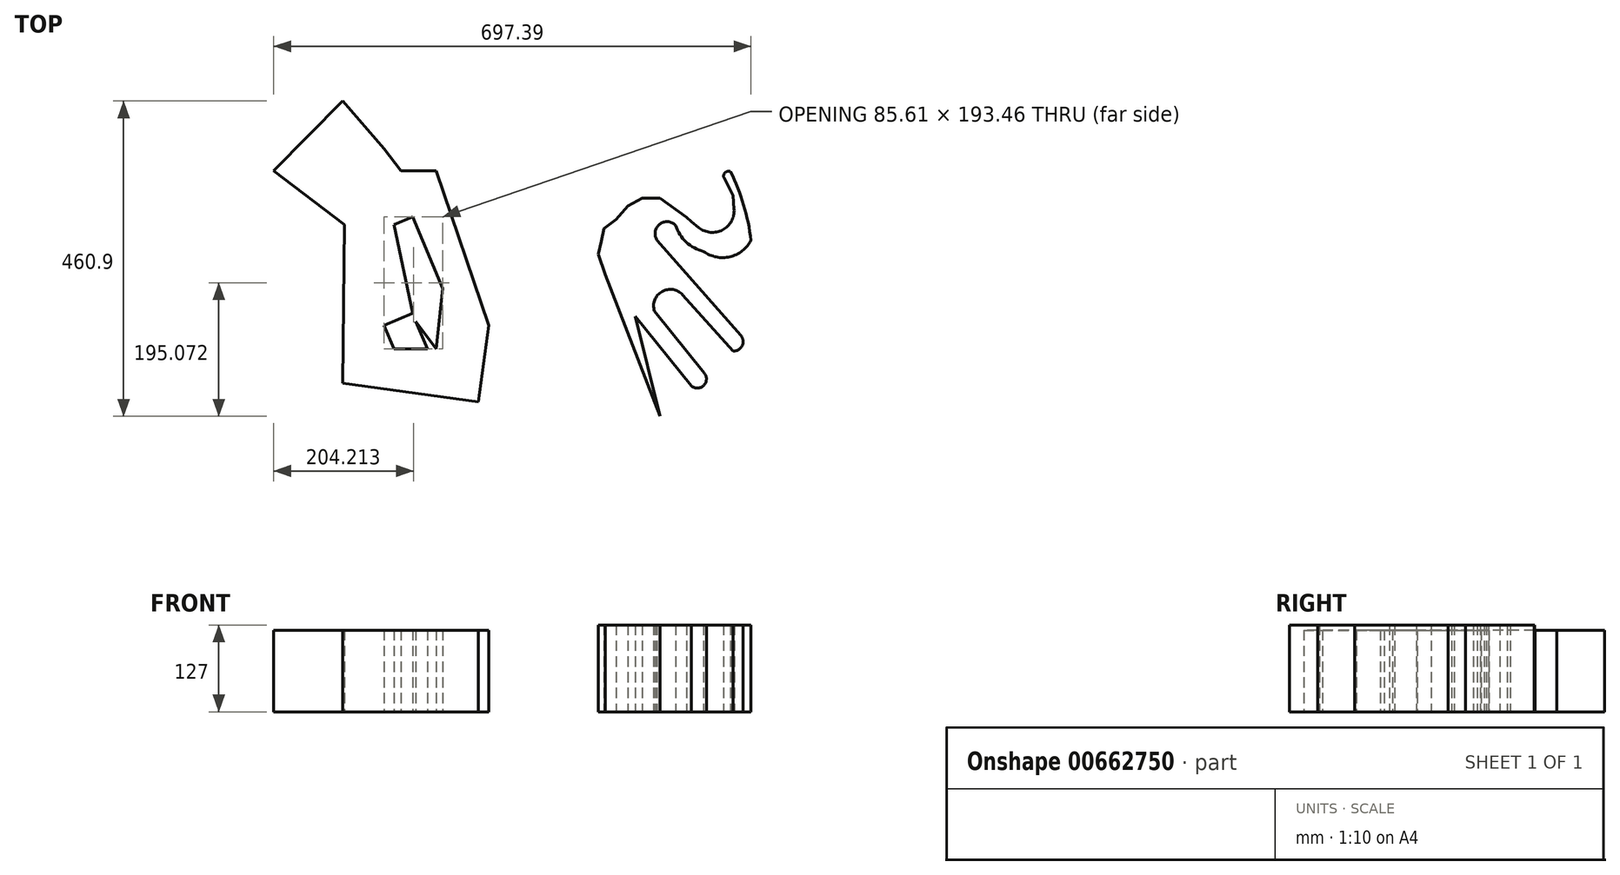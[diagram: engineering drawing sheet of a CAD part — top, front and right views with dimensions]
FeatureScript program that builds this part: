
annotation { "Feature Type Name" : "Feature", "Feature Type Description" : "" }
export const myFeature = defineFeature(function(context is Context, id is Id, definition is map)
    precondition{}
    {
        {
            var Q0;
            Q0=qCreatedBy(makeId("Top.planeOp"),FACE);
            var sketch = newSketch(context, id + "F0", { "sketchPlane" : qUnion([Q0])});
            skLineSegment(sketch, "E0", {"start": v(47.23, 61.57) * mm, "end": v(53.85, 55.23) * mm});
            skLineSegment(sketch, "E1", {"start": v(53.85, 55.23) * mm, "end": v(64.9, 46.36) * mm});
            skArc(sketch, "E2", {"start": v(64.9, 46.36) * mm, "mid": v(99.64, 43.04) * mm, "end": v(116.5, 73.6) * mm});
            skLineSegment(sketch, "E3", {"start": v(116.5, 73.6) * mm, "end": v(114.97, 93.25) * mm});
            skLineSegment(sketch, "E4", {"start": v(114.97, 93.25) * mm, "end": v(101.97, 118.57) * mm});
            skArc(sketch, "E5", {"start": v(111.25, 128.16) * mm, "mid": v(103.17, 126.7) * mm, "end": v(101.97, 118.57) * mm});
            skArc(sketch, "E6", {"start": v(141.26, 27.78) * mm, "mid": v(130.43, 79.22) * mm, "end": v(111.25, 128.16) * mm});
            skArc(sketch, "E7", {"start": v(71.92, 11.46) * mm, "mid": v(110.32, 3.76) * mm, "end": v(141.26, 27.78) * mm});
            skArc(sketch, "E8", {"start": v(31.18, 49.76) * mm, "mid": v(46.48, 25.22) * mm, "end": v(71.92, 11.46) * mm});
            skArc(sketch, "E9", {"start": v(31.18, 49.76) * mm, "mid": v(7.54, 51.2) * mm, "end": v(3.97, 27.78) * mm});
            skLineSegment(sketch, "E10", {"start": v(3.97, 27.78) * mm, "end": v(126.28, -111.28) * mm});
            skArc(sketch, "E11", {"start": v(114.82, -133.98) * mm, "mid": v(128.22, -126.5) * mm, "end": v(126.28, -111.28) * mm});
            skLineSegment(sketch, "E12", {"start": v(114.82, -133.98) * mm, "end": v(41.23, -51.98) * mm});
            skArc(sketch, "E13", {"start": v(41.23, -51.98) * mm, "mid": v(11.1, -47.12) * mm, "end": v(0, -75.54) * mm});
            skLineSegment(sketch, "E14", {"start": v(0, -75.54) * mm, "end": v(73.08, -166.55) * mm});
            skArc(sketch, "E15", {"start": v(54.15, -185.1) * mm, "mid": v(72.02, -184.4) * mm, "end": v(73.08, -166.55) * mm});
            skLineSegment(sketch, "E16", {"start": v(54.15, -185.1) * mm, "end": v(-27.85, -83.4) * mm});
            skLineSegment(sketch, "E17", {"start": v(-27.85, -83.4) * mm, "end": v(-71.92, -22.47) * mm});
            skLineSegment(sketch, "E18", {"start": v(-71.92, -22.47) * mm, "end": v(-81.6, 7.5) * mm});
            skLineSegment(sketch, "E19", {"start": v(-81.6, 7.5) * mm, "end": v(-77.5, 26.8) * mm});
            skLineSegment(sketch, "E20", {"start": v(-77.5, 26.8) * mm, "end": v(-73.68, 45.1) * mm});
            skLineSegment(sketch, "E21", {"start": v(-73.68, 45.1) * mm, "end": v(-56.1, 58.65) * mm});
            skLineSegment(sketch, "E22", {"start": v(-56.1, 58.65) * mm, "end": v(-38.53, 78.1) * mm});
            skLineSegment(sketch, "E23", {"start": v(-38.53, 78.1) * mm, "end": v(-17.84, 89.2) * mm});
            skLineSegment(sketch, "E24", {"start": v(-17.84, 89.2) * mm, "end": v(8.08, 89.2) * mm});
            skLineSegment(sketch, "E25", {"start": v(8.08, 89.2) * mm, "end": v(47.23, 61.57) * mm});
            skLineSegment(sketch, "E26", {"start": v(-71.92, -22.47) * mm, "end": v(8.08, -229.5) * mm});
            skLineSegment(sketch, "E27", {"start": v(8.08, -229.5) * mm, "end": v(-27.85, -83.4) * mm});
            skSolve(sketch);
        }
        {
            var Q0;
            Q0=makeQuery(id+"F0.imprint","IMPRINT",FACE,{"disambiguationData":[TD([[makeQuery(id+"F0.imprint","IMPRINT",EDGE,{"derivedFrom":sQuery(id+"F0.wireOp",EDGE,"E17")}),1.0]])]});
            var Q1;
            Q1=makeQuery(id+"F0.imprint","IMPRINT",FACE,{"disambiguationData":[TD([[makeQuery(id+"F0.imprint","IMPRINT",EDGE,{"derivedFrom":sQuery(id+"F0.wireOp",EDGE,"E0")}),-1.0]])]});
            extrude(context, id + "F1", {"entities" : qUnion([Q0, Q1]), "depth" : 127 * mm, "offsetDistance" : 25.4 * mm});
        }
        {
            var Q0;
            Q0=qCreatedBy(makeId("Top.planeOp"),FACE);
            var sketch = newSketch(context, id + "F2", { "sketchPlane" : qUnion([Q0])});
            skLineSegment(sketch, "E28", {"start": v(-380.09, -131.16) * mm, "end": v(-394.72, -96.47) * mm});
            skLineSegment(sketch, "E29", {"start": v(-394.72, -96.47) * mm, "end": v(-353.36, -79.02) * mm});
            skLineSegment(sketch, "E30", {"start": v(-353.36, -79.02) * mm, "end": v(-331.37, -131.16) * mm});
            skLineSegment(sketch, "E31", {"start": v(-380.09, -131.16) * mm, "end": v(-331.37, -131.16) * mm});
            skLineSegment(sketch, "E32", {"start": v(-353.36, -79.02) * mm, "end": v(-380.09, 51.03) * mm});
            skLineSegment(sketch, "E33", {"start": v(-380.09, 51.03) * mm, "end": v(-353.36, 62.3) * mm});
            skLineSegment(sketch, "E34", {"start": v(-353.36, 62.3) * mm, "end": v(-309.1, -42.59) * mm});
            skLineSegment(sketch, "E35", {"start": v(-309.1, -42.59) * mm, "end": v(-318.63, -131.16) * mm});
            skLineSegment(sketch, "E36", {"start": v(-318.63, -131.16) * mm, "end": v(-452.95, 51.03) * mm});
            skLineSegment(sketch, "E37", {"start": v(-452.95, 51.03) * mm, "end": v(-440.07, 136.19) * mm});
            skLineSegment(sketch, "E38", {"start": v(-440.07, 136.19) * mm, "end": v(-394.72, 129.33) * mm});
            skLineSegment(sketch, "E39", {"start": v(-394.72, 129.33) * mm, "end": v(-318.63, 129.33) * mm});
            skLineSegment(sketch, "E40", {"start": v(-318.63, 129.33) * mm, "end": v(-241.71, -96.47) * mm});
            skLineSegment(sketch, "E41", {"start": v(-241.71, -96.47) * mm, "end": v(-257.23, -208.52) * mm});
            skLineSegment(sketch, "E42", {"start": v(-257.23, -208.52) * mm, "end": v(-455.52, -181.06) * mm});
            skLineSegment(sketch, "E43", {"start": v(-559.02, 136.19) * mm, "end": v(-556.13, 129.33) * mm});
            skLineSegment(sketch, "E44", {"start": v(-455.52, 231.4) * mm, "end": v(-394.72, 161.56) * mm});
            skLineSegment(sketch, "E45", {"start": v(-394.72, 161.56) * mm, "end": v(-452.95, 51.03) * mm});
            skLineSegment(sketch, "E46", {"start": v(-455.52, -181.06) * mm, "end": v(-452.95, 51.03) * mm});
            skLineSegment(sketch, "E47", {"start": v(-556.13, 129.33) * mm, "end": v(-452.95, 51.03) * mm});
            skLineSegment(sketch, "E48", {"start": v(-556.13, 129.33) * mm, "end": v(-455.52, 231.4) * mm});
            skLineSegment(sketch, "E49", {"start": v(-394.72, 161.56) * mm, "end": v(-296.83, 32.85) * mm});
            skLineSegment(sketch, "E50", {"start": v(-318.63, -131.16) * mm, "end": v(-296.83, 32.85) * mm});
            skSolve(sketch);
        }
        {
            var Q0;
            Q0 = qSketchRegion(id + "F2", true);
            extrude(context, id + "F3", {"entities" : qUnion([Q0]), "depth" : 119.38 * mm, "offsetDistance" : 25.4 * mm});
        }
    });
